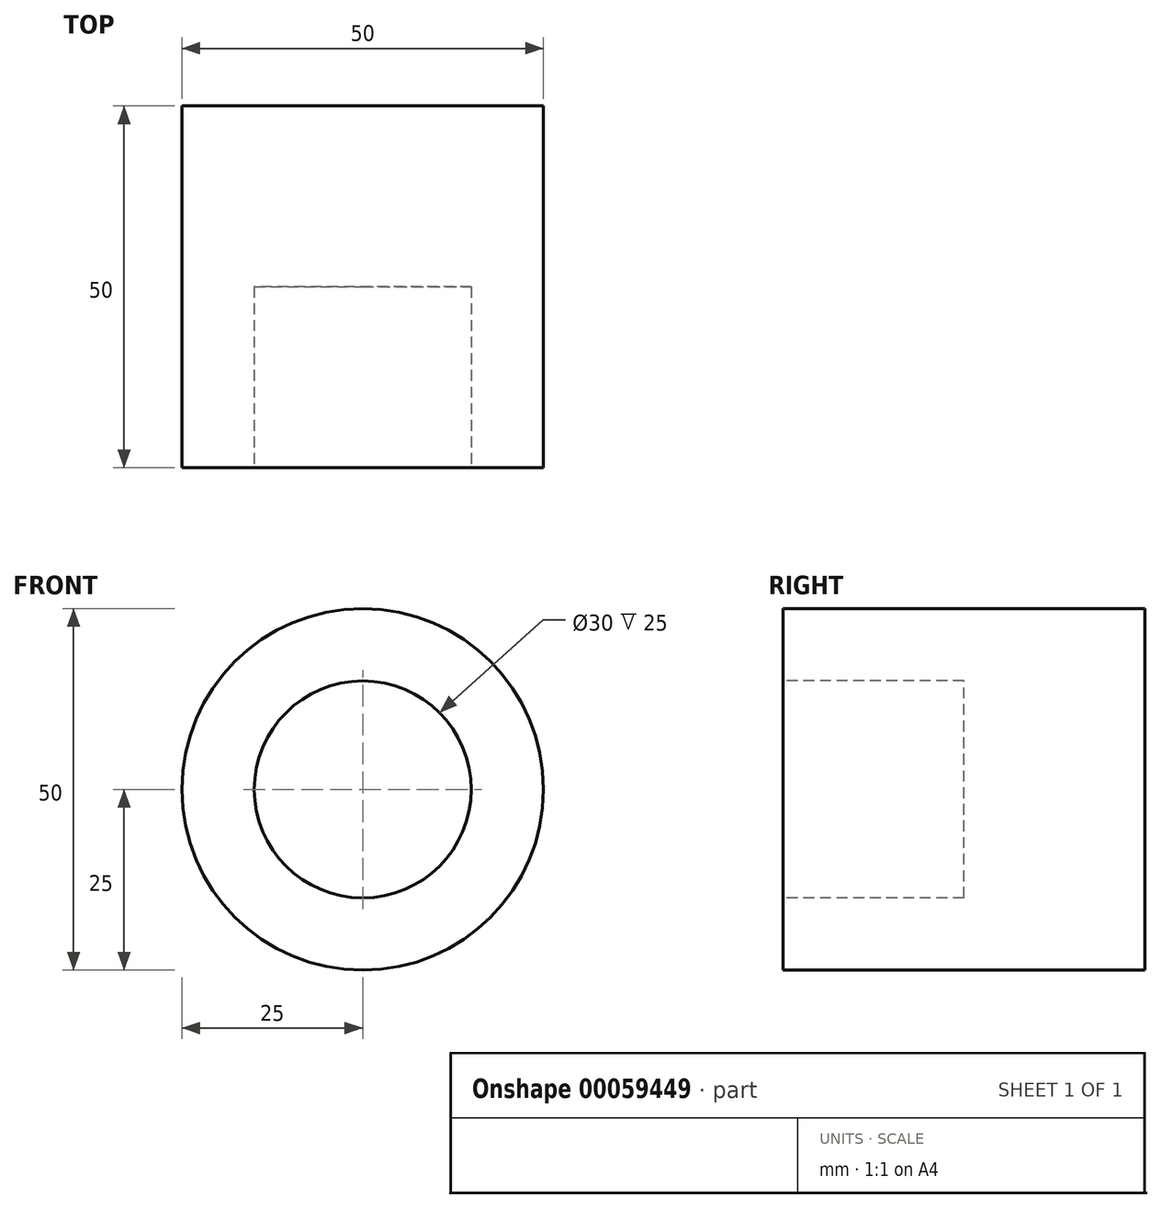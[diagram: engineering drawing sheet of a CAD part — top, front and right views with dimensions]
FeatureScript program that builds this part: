
annotation { "Feature Type Name" : "Feature", "Feature Type Description" : "" }
export const myFeature = defineFeature(function(context is Context, id is Id, definition is map)
    precondition{}
    {
        {
            var Q0;
            Q0=qCreatedBy(makeId("Front.planeOp"),FACE);
            var sketch = newSketch(context, id + "F0", { "sketchPlane" : qUnion([Q0])});
            skCircle(sketch, "E0", {"center": v(0, 0) * mm, "radius": 25 * mm});
            skSolve(sketch);
        }
        {
            var Q0;
            Q0 = qSketchRegion(id + "F0", true);
            var Q1;
            Q1=sQuery(id+"F0.wireOp",EDGE,"E0");
            var Q2;
            Q2 = qBodyType(qCreatedBy(id + "F0" ,EDGE), BodyType.WIRE);
            extrude(context, id + "F1", {"entities" : qUnion([Q0]), "surfaceEntities" : qUnion([Q1, Q2]), "oppositeDirection" : true, "depth" : 50 * mm});
        }
        {
            var Q0;
            Q0=makeQuery(id+"F1.opExtrude","CAP_FACE",FACE,{"disambiguationData":[OSD([sQuery(id+"F0.wireOp",EDGE,"E0")])],"isStart":true});
            var sketch = newSketch(context, id + "F2", { "sketchPlane" : qUnion([Q0])});
            skCircle(sketch, "E1", {"center": v(0, 0) * mm, "radius": 15 * mm});
            skSolve(sketch);
        }
        {
            var Q0;
            Q0=makeQuery(id+"F2.imprint","IMPRINT",FACE,{"disambiguationData":[TD([[makeQuery(id+"F2.imprint","IMPRINT",EDGE,{"derivedFrom":sQuery(id+"F2.wireOp",EDGE,"E1")}),1.0]])]});
            extrude(context, id + "F3", {"entities" : qUnion([Q0]), "operationType" : NewBodyOperationType.REMOVE, "oppositeDirection" : true, "depth" : 25 * mm});
        }
    });
